# Revit family: Мультибиометрический терминал распознавания лиц, вен ладони, карт RFID (Linux)_SpeedFace-V5L-RFID WiFi
name_source: partatom
category: Охранная сигнализация
units: mm (PartAtom-declared; Revit-internal decimal feet)

## family parameters
Всегда вертикально = Нет
На основе рабочей плоскости = Нет
Общий = Да
При загрузке вырезать с полостями = Нет
Размер круглого соединителя = Использовать диаметр
Сохранять ориентацию аннотаций = Нет
Тип детали = Нормальный
Точка расчета площади = Да

## types (3) — shared parameters
=Габариты= = =Габариты=
ADSK_Единица измерения = шт.
ADSK_Завод-изготовитель = TemID
ADSK_Количество = 1
ADSK_Обозначение = RD
ADSK_Раздел спецификации = 3. Периферийное оборудование
ADSK_Размер_Высота = 203 мм
ADSK_Размер_Глубина = 22 мм
ADSK_Размер_Ширина = 92 мм
URL = https://temid-global.ru
Зона обслуживания_Отступ от прибора = 50 мм
Материал = Светло-серый
УГО_Тип = УГО_СКУД_Считыватель
zero-valued in all types: Отметка по умолчанию

## per-type parameters (varying)
| type | ADSK_Марка | ADSK_Наименование | ADSK_Тип |
| SpeedFace-V5L | SpeedFace-V5L | Мультибиометрический терминал распознавания лиц (Linux) | SpeedFace-V5L |
| SpeedFace-V5L-RFID | SF-V5L-RFID | Мультибиометрический терминал распознавания лиц, вен ладони и карт | SF-V5L-RFID |
| SpeedFace-V5L-RFID WiFi | SF-V5L-RFID WiFi | Мультибиометрический терминал распознавания лиц, вен ладони, карт RFID (Linux) | SF-V5L-RFID WiFi |
